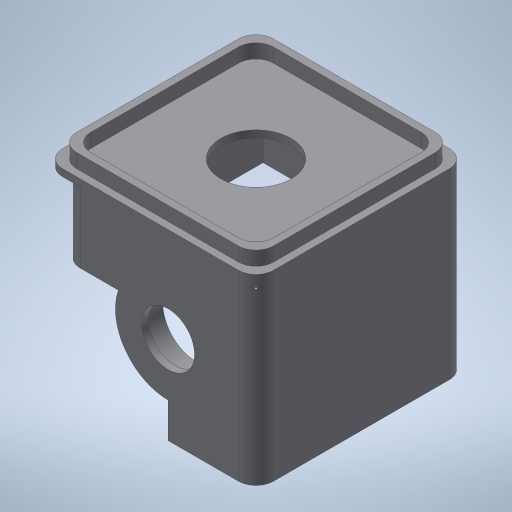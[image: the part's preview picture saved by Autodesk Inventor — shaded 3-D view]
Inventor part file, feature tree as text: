
AUTODESK INVENTOR PART (.ipt)
format: ipt  version: 2023.1 (Build 271208000, 208)  size: 475,648 bytes
history: native  units: mm
features: sketch x19, extrude x15, projected_geometry x14, hole x3, fillet x1
ambient origin geometry x8: Origin, YZ Plane, XZ Plane, XY Plane, X Axis, Y Axis, Z Axis, Center Point
bodies: Solid1 (feature_tree)
feature tree (52):
  extrude  "Extrusion1"  Depth=60.0mm
  extrude  "Extrusion2"  Depth=2.0mm
  hole  "Hole1"  [1 undecoded]
  extrude  "Extrusion3"  Depth=50.0mm
  extrude  "Extrusion4"  Depth=50.0mm
  extrude  "Extrusion5"  Depth=5.0mm
  extrude  "Extrusion6"  Depth=10.0mm
  extrude  "Extrusion7"  Depth=15.0mm
  hole  "Hole2"  [1 undecoded]
  hole  "Hole3"  [1 undecoded]
  extrude  "Extrusion8"  Depth=30.0mm
  extrude  "Extrusion9"  Depth=8.0mm
  sketch  "Sketch13"  dims[d33=8.0mm d34=0.0mm d35=1.5mm]
  extrude  "Extrusion10"  Depth=30.0mm
  extrude  "Extrusion11"  TaperAngle=120.0deg  [1 undecoded]
  extrude  "Extrusion12"  TaperAngle=30.0deg  [1 undecoded]
  extrude  "Extrusion13"  Depth=5.0mm TaperAngle=0.0deg
  extrude  "Extrusion14"  Depth=2.0mm
  extrude  "Extrusion15"  Depth=6.0mm TaperAngle=0.0deg
  fillet  "Fillet1"  Radius=2.0mm
  sketch  "Sketch1"  dims[d0=60.0mm d1=60.0mm]
  sketch  "Sketch2"  dims[d2=2.0mm d3=0.0mm d4=2.0mm]
  projected_geometry  "Projected Loop1"
  sketch  "Sketch3"  dims[d5=2.0mm d6=4.0mm d7=0.0mm]
  sketch  "Sketch4"  dims[d8=20.0mm]
  projected_geometry  "Projected Loop2"
  sketch  "Sketch5"  dims[d9=20.0mm d10=6.0mm d11=4.0mm d12=2.0mm d13=90.0deg d14=8.0mm d15=20.594885mm d16=50.0mm]
  projected_geometry  "Projected Loop3"
  sketch  "Sketch6"  dims[d17=8.0mm d18=50.0mm]
  projected_geometry  "Projected Loop4"
  sketch  "Sketch7"  dims[d19=8.0mm d20=5.0mm]
  projected_geometry  "Projected Loop5"
  sketch  "Sketch8"  dims[d21=10.0mm d22=0.0mm d23=10.0mm]
  sketch  "Sketch9"  dims[d24=15.0mm d25=15.0mm]
  projected_geometry  "Projected Loop6"
  sketch  "Sketch10"  dims[d26=30.0mm d27=8.0mm d28=0.0mm]
  projected_geometry  "Projected Loop7"
  sketch  "Sketch11"  dims[d29=10.0mm d30=15.0mm]
  projected_geometry  "Projected Loop8"
  sketch  "Sketch12"  dims[d31=15.0mm d32=30.0mm]
  projected_geometry  "Projected Loop9"
  sketch  "Sketch14"  dims[d36=2.0mm d37=30.0mm]
  projected_geometry  "Projected Loop10"
  sketch  "Sketch15"  dims[d38=150.0deg d39=120.0deg]
  projected_geometry  "Projected Loop11"
  sketch  "Sketch16"  dims[d40=60.0deg d41=30.0deg]
  sketch  "Sketch17"  dims[d42=5.0mm d43=0.0mm]
  projected_geometry  "Projected Loop12"
  sketch  "Sketch18"  dims[d44=1.5mm d45=2.0mm d46=30.0mm d47=150.0deg d48=120.0deg d49=60.0deg d50=30.0deg d51=5.0mm d52=0.0mm]
  projected_geometry  "Projected Loop13"
  sketch  "Sketch19"  dims[d53=15.0mm d54=15.0mm d55=6.0mm d56=4.0mm d57=2.0mm d58=90.0deg d59=8.0mm d60=20.594885mm d61=15.0mm d62=6.0mm d63=4.0mm d64=2.0mm d65=90.0deg d66=8.0mm d67=20.594885mm d68=2.0mm d69=6.0mm d70=0.0mm d71=2.0mm d72=6.0mm d73=0.0mm d74=25.0mm d75=40.0mm d76=8.0mm d77=0.0mm d78=8.0mm d79=0.0mm d80=40.0mm d81=0.0mm d82=5.0mm d83=60.0mm d84=20.0mm d85=0.0mm d86=8.0mm d87=0.0mm d88=8.0mm d89=0.0mm d90=5.0mm]
  projected_geometry  "Projected Loop14"
note: 5 required parameter values undecoded (feature->parameter linkage not recoverable at this tier; creation-order binding heuristic only, values carry confidence <= 0.55)
